# Revit family: STL22951BR_30_40_50_STL22951PTO_30_40
name_source: partatom
category: Luminárias
units: mm (PartAtom-declared; Revit-internal decimal feet)

## family parameters
Compartilhado = Não
Corte com vazios quando carregada = Não
Cota do conector redondo = Utilizar diâmetro
Fonte luminosa = Sim
Hospedeiro = Forro
Manter orientação da anotação = Não
Número OmniClass = 23.80.70.11
Ponto de cálculo do ambiente = Não
Sempre na vertical = Sim
Tipo de parte = Normal
Título OmniClass = Luminaries for Internal Lighting

## types (5) — shared parameters
Altura = 0.05 m
Comprimento = 0.17 m
Dimerização = Não dimerizável
Fabricante = Stella
Filtro de cor = 16777215
Fluxo Luminoso = 900 lm
Grau de proteção (IP) = IP20
IRC (Índice de reprodução de cores) = >80
Largura = 0.17 m
Modelo = EDGE
Potência = 8 W
Tensão Elétrica = 100V-240V
Troca de temperatura da cor de lâmpada com esmaecimento = <Nenhum>
URL = https://stella.com.br
Ângulo de Abertura = 110°
Ângulo de inclinação = 90.00°
zero-valued in all types: Elevação padrão

## per-type parameters (varying)
| type | Arquivo de rede fotométrica | Estrutura | Luminoso | Referência | Temperatura da cor (K) |
| STL22951BR/30 - BRANCO - BIVOLT - 3000K - 900lm - 110° | STELLA - STL22951BR-30 - EDGE 8W.ies | Al - Branco | Luminoso - 3000K | STL22951BR/30 - BRANCO - BIVOLT | 3000 K |
| STL22951PTO/30 - PRETO - BIVOLT - 3000K - 900lm - 110° | STELLA - STL22951PTO-30 - EDGE 8W.ies | Al - Preto | Luminoso - 3000K | STL22951PTO/30 - PRETO - BIVOLT | 3000 K |
| STL22951BR/40 - BRANCO - BIVOLT - 4000K - 900lm - 110° | STELLA - STL22951BR-40 - EDGE 8W.ies | Al - Branco | Luminoso - 4000K | STL22951BR/40 - BRANCO - BIVOLT | 4000 K |
| STL22951PTO/40 - PRETO - BIVOLT - 4000K - 900lm - 110° | STELLA - STL22951PTO-40 - EDGE 8W.ies | Al - Preto | Luminoso - 4000K | STL22951PTO/40 - PRETO - BIVOLT | 4000 K |
| STL22951BR/50 - BRANCO - BIVOLT - 5000K - 900lm - 110° | STELLA - STL22951BR-50 - EDGE 8W.ies | Al - Branco | Luminoso - 5000K | STL22951BR/50 - BRANCO - BIVOLT | 5000 K |
